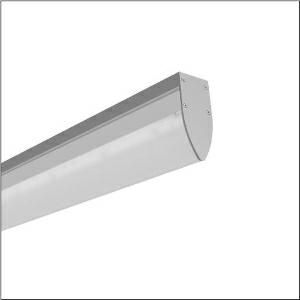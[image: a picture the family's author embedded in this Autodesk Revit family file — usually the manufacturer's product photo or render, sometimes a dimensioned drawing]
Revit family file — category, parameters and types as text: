
# Revit family: mira_r__21_td_51fr527g454a_bdf0
name_source: partatom
category: Lighting Fixtures
units: mm (PartAtom-declared; Revit-internal decimal feet)

## family parameters
Cut with Voids When Loaded = No
Host = Face
Light Source = No
Part Type = Normal
Room Calculation Point = No
Round Connector Dimension = Use Diameter
Shared = No

## types (1)
- Mira® 21 TD (1 x LED, 5500 lm, 39 W, 4000K)
    Apparent Load = 39 VA
    CIE Flux Codes = 40 68 87 81 100
    Color Rendering = 80
    Color Temperature = 4000K
    Default Elevation = 1800 mm
    Description = Mira® 21 TD, clean room luminaire, primary light control with reflector, primary optical cover: cover, of PMMA, frosted, light emission: direct distribution, primary light characteristic: symmetric, installation type: surface-mounted, LED, rated luminous flux: 5.500lm, luminous efficacy: 141lm/W, light colour: 840, colour temperature: 4000K, control gear: ECG, with terminal, 3-pole, max. 2.5mm², mains connection: 230V, AC, 50/60Hz, rated input power: 39W, luminaire housing, of sheet steel, coated, pure white, length: 900mm, width: 55mm, height: 120mm, protection rating (complete): IP43, insulation class (complete): insulation class I (protective earthing), certification: CE, UKCA, permissible operating ambient temperature: -5..+40°C, standard: EN 50419, packaging unit: 1 piece
    Height = 0 mm  [stored 0 ft]
    Lamp = 1 x LED
    Lamp Light Flux = 5500 lm
    Lamp Power = 39 W
    Lamp count = 1
    Length = 900 mm
    Luminous efficacy = 141 lm/W
    Manufacturer = Siteco
    ModVariant = No
    Model = 51FR527G454A
    Mounting Place = Ceiling
    Mounting Type = Recessed
    Number of Poles = 1
    OnlyDefault = Yes
    Power Factor = 1
    Product Name = Mira® 21 TD
    Product group = clean room luminaire
    ProductGroupID = 401
    Protection Class = Protection class I
    Protection Degree = IP 43
    RLX_Detail_Level = 1
    RlxData = <blob elided: 25121 chars, md5=f8db9033>
    Socket = socket
    Standby Power = 0 W
    System Light Flux = 5500 lm
    System Power = 39 W
    Type Comments = Product without accessories
    Type Image = l_1007115.jpg
    URL = http://relux.com
    VarID = ---
    Voltage = 0 V
    Weight = 0.00 kg
    Width = 55 mm

note: [stored X ft] marks values corroborated as IEEE doubles in the binary element streams (Revit-internal decimal feet)

## geometry (parser evidence)
native form markers: Blend x4, Sweep x12
no freeform markers — native parametric forms only
